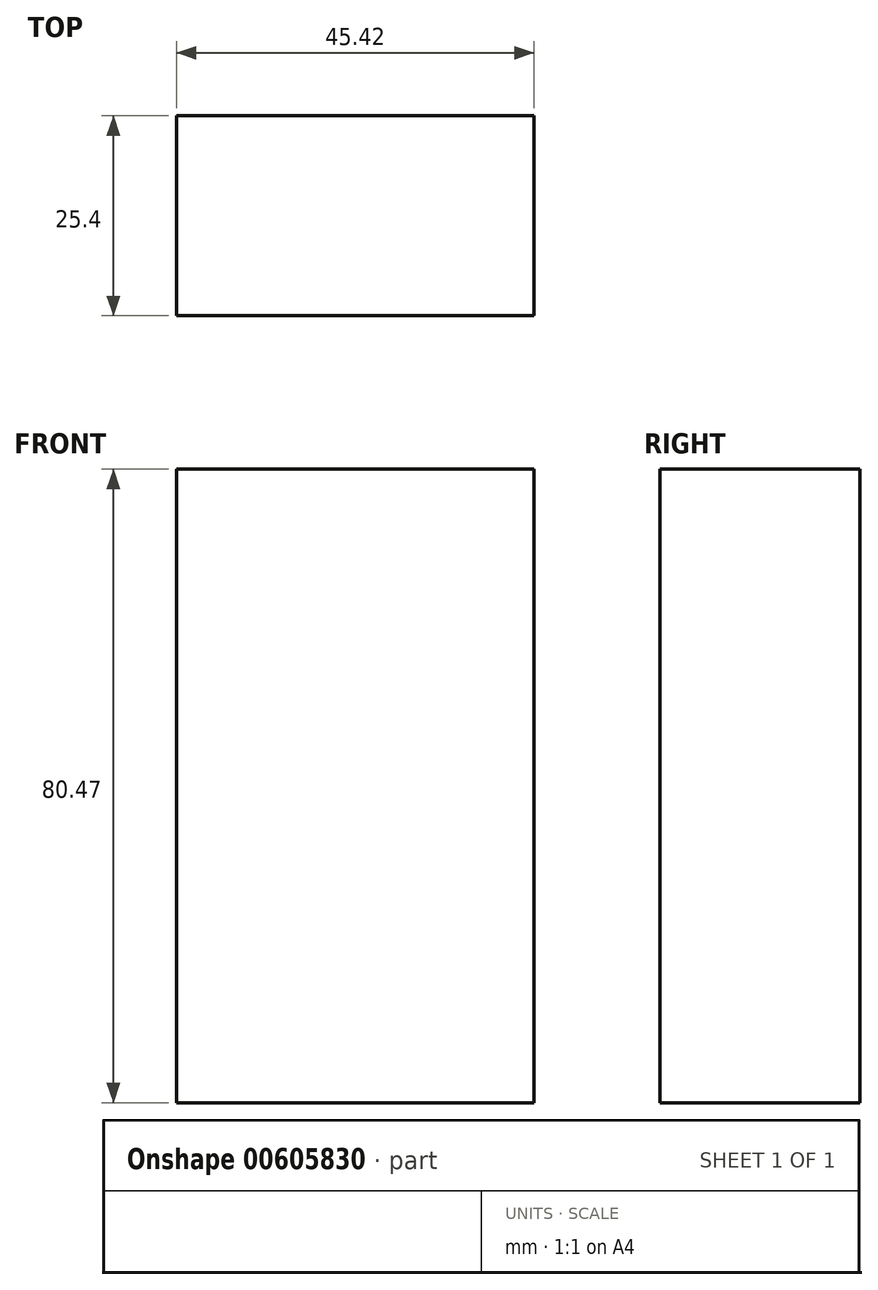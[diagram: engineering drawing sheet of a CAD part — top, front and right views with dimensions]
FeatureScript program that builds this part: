
annotation { "Feature Type Name" : "Feature", "Feature Type Description" : "" }
export const myFeature = defineFeature(function(context is Context, id is Id, definition is map)
    precondition{}
    {
        {
            var Q0;
            Q0=qCreatedBy(makeId("Front.planeOp"),FACE);
            var sketch = newSketch(context, id + "F0", { "sketchPlane" : qUnion([Q0])});
            skLineSegment(sketch, "E0", {"start": v(-22.7, 35.66) * mm, "end": v(-22.7, -44.8) * mm});
            skLineSegment(sketch, "E1", {"start": v(-22.7, 35.66) * mm, "end": v(22.7, 35.66) * mm});
            skLineSegment(sketch, "E2", {"start": v(22.7, 35.66) * mm, "end": v(22.7, -44.8) * mm});
            skLineSegment(sketch, "E3", {"start": v(-22.7, -44.8) * mm, "end": v(22.7, -44.8) * mm});
            skSolve(sketch);
        }
        {
            var Q0;
            Q0 = qSketchRegion(id + "F0", true);
            extrude(context, id + "F1", {"entities" : qUnion([Q0]), "depth" : 25.4 * mm, "offsetDistance" : 25.4 * mm});
        }
    });
